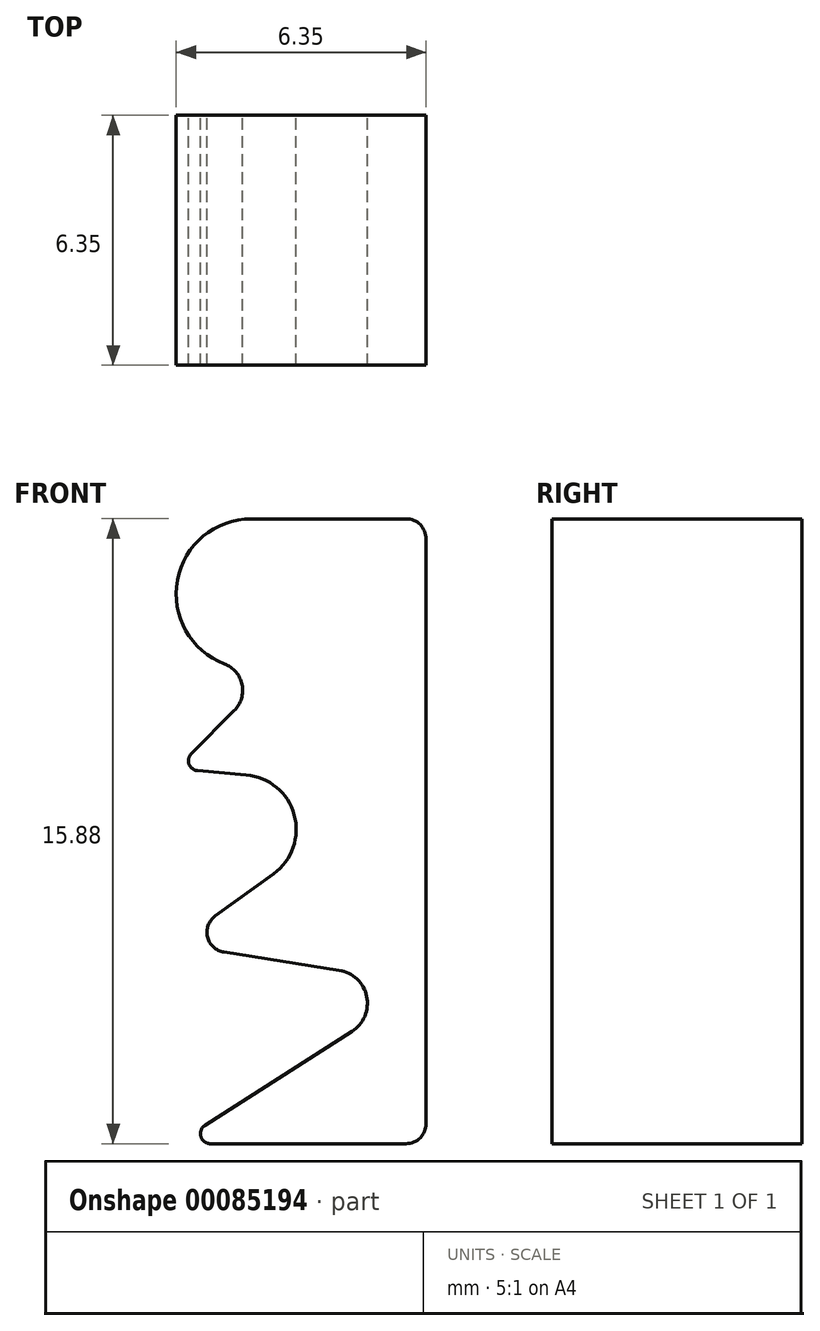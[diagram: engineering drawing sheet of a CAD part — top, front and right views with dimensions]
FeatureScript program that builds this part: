
annotation { "Feature Type Name" : "Feature", "Feature Type Description" : "" }
export const myFeature = defineFeature(function(context is Context, id is Id, definition is map)
    precondition{}
    {
        {
            var Q0;
            Q0=qCreatedBy(makeId("Front.planeOp"),FACE);
            var sketch = newSketch(context, id + "F0", { "sketchPlane" : qUnion([Q0])});
            skLineSegment(sketch, "E0.bottom", {"start": v(0, 0) * mm, "end": v(6.35, 0) * mm});
            skLineSegment(sketch, "E0.top", {"start": v(0, 15.88) * mm, "end": v(6.35, 15.88) * mm});
            skLineSegment(sketch, "E0.left", {"start": v(0, 0) * mm, "end": v(0, 15.87) * mm, "construction": true});
            skLineSegment(sketch, "E0.right", {"start": v(6.35, 0) * mm, "end": v(6.35, 15.87) * mm});
            skLineSegment(sketch, "E1", {"start": v(0, 15.88) * mm, "end": v(6.35, 0) * mm, "construction": true});
            skLineSegment(sketch, "E2", {"start": v(1.48, 11) * mm, "end": v(0, 9.52) * mm});
            skLineSegment(sketch, "E3", {"start": v(2.48, 6.86) * mm, "end": v(0, 5.06) * mm});
            skLineSegment(sketch, "E4", {"start": v(0, 5.06) * mm, "end": v(4.14, 4.4) * mm});
            skLineSegment(sketch, "E5", {"start": v(0, 9.52) * mm, "end": v(1.78, 9.37) * mm});
            skArc(sketch, "E6", {"start": v(4.47, 2.85) * mm, "mid": v(4.84, 3.74) * mm, "end": v(4.14, 4.4) * mm});
            skArc(sketch, "E7", {"start": v(2.48, 6.86) * mm, "mid": v(3, 8.36) * mm, "end": v(1.78, 9.37) * mm});
            skArc(sketch, "E8", {"start": v(1.9, 15.88) * mm, "mid": v(0.03, 14.32) * mm, "end": v(1.22, 12.2) * mm});
            skArc(sketch, "E9", {"start": v(1.48, 11) * mm, "mid": v(1.67, 11.66) * mm, "end": v(1.22, 12.2) * mm});
            skLineSegment(sketch, "E10.trimOffspring", {"start": v(4.47, 2.85) * mm, "end": v(0, 0) * mm});
            skSolve(sketch);
        }
        {
            var Q0;
            Q0 = qSketchRegion(id + "F0", true);
            extrude(context, id + "F1", {"entities" : qUnion([Q0]), "depth" : 6.35 * mm});
        }
        {
            var Q0;
            Q0=makeQuery(id+"F1.opExtrude","SWEPT_EDGE",EDGE,{"disambiguationData":[OSD([sQuery(id+"F0.wireOp",EDGE,"E0.bottom"),sQuery(id+"F0.wireOp",EDGE,"E10.trimOffspring")])]});
            var Q1;
            Q1=makeQuery(id+"F1.opExtrude","SWEPT_EDGE",EDGE,{"disambiguationData":[OSD([sQuery(id+"F0.wireOp",EDGE,"E2"),sQuery(id+"F0.wireOp",EDGE,"E5")])]});
            fillet(context, id + "F2", {"entities" : qUnion([Q0, Q1]), "radius" : 0.25 * mm, "tangentPropagation" : true, "allowEdgeOverflow" : false});
        }
        {
            var Q0;
            Q0=makeQuery(id+"F1.opExtrude","SWEPT_EDGE",EDGE,{"disambiguationData":[OSD([sQuery(id+"F0.wireOp",EDGE,"E0.bottom"),sQuery(id+"F0.wireOp",EDGE,"E0.right")])]});
            var Q1;
            Q1=makeQuery(id+"F1.opExtrude","SWEPT_EDGE",EDGE,{"disambiguationData":[OSD([sQuery(id+"F0.wireOp",EDGE,"E0.top"),sQuery(id+"F0.wireOp",EDGE,"E0.right")])]});
            var Q2;
            Q2=makeQuery(id+"F1.opExtrude","SWEPT_EDGE",EDGE,{"disambiguationData":[OSD([sQuery(id+"F0.wireOp",EDGE,"E3"),sQuery(id+"F0.wireOp",EDGE,"E4")])]});
            fillet(context, id + "F3", {"entities" : qUnion([Q0, Q1, Q2]), "radius" : 0.5 * mm, "tangentPropagation" : true, "allowEdgeOverflow" : false});
        }
    });
